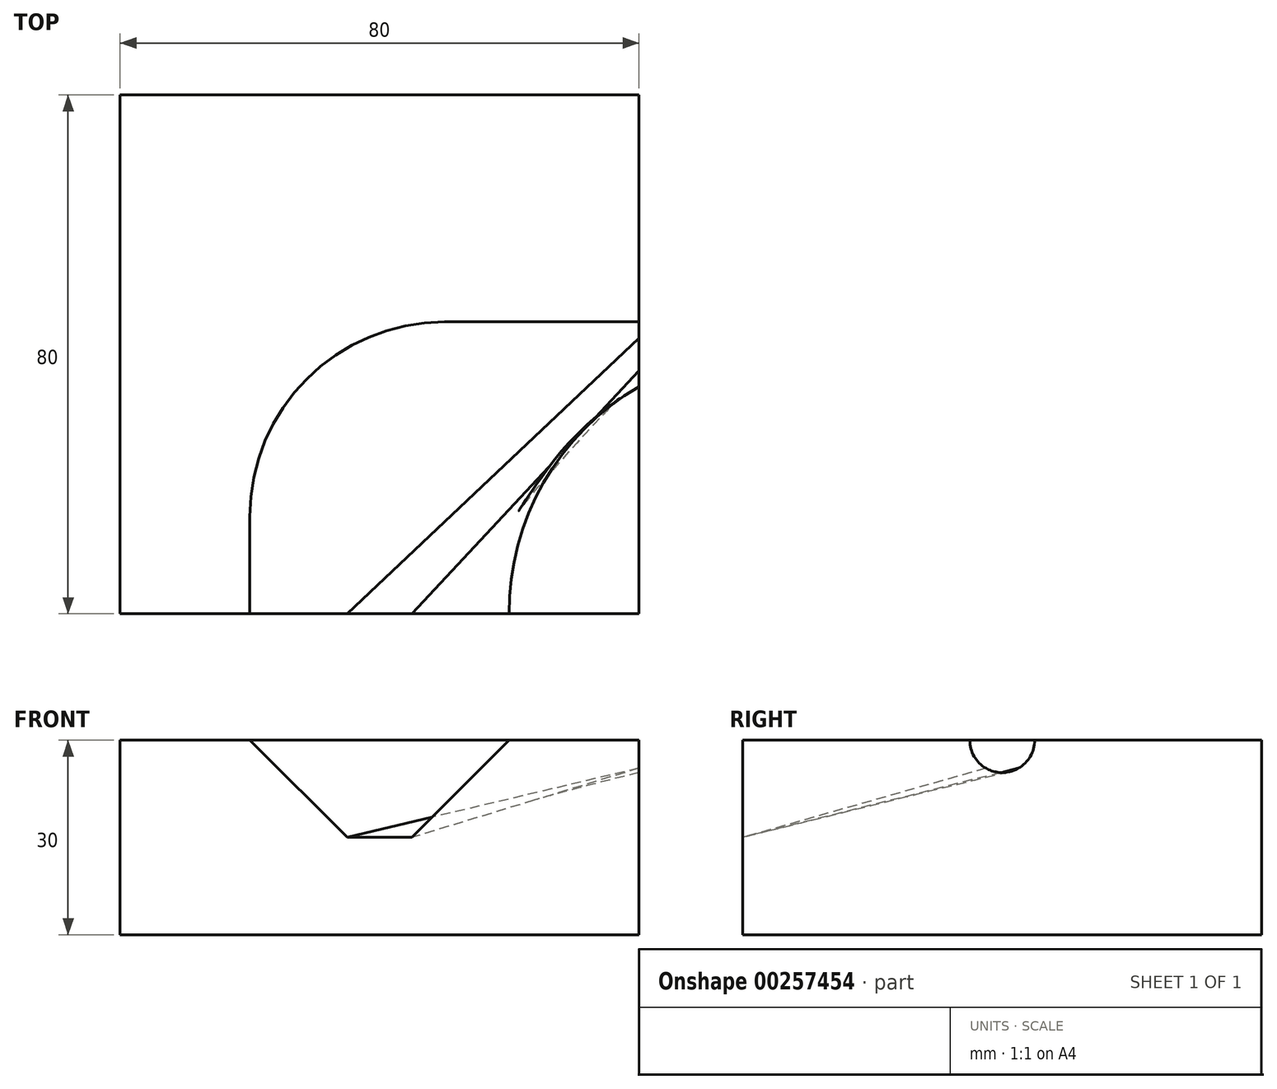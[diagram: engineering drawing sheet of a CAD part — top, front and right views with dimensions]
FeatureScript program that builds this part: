
annotation { "Feature Type Name" : "Feature", "Feature Type Description" : "" }
export const myFeature = defineFeature(function(context is Context, id is Id, definition is map)
    precondition{}
    {
        {
            var Q0;
            Q0=qCreatedBy(makeId("Top.planeOp"),FACE);
            var sketch = newSketch(context, id + "F0", { "sketchPlane" : qUnion([Q0])});
            skLineSegment(sketch, "E0.bottom", {"start": v(40, 40) * mm, "end": v(-40, 40) * mm});
            skLineSegment(sketch, "E0.top", {"start": v(40, -40) * mm, "end": v(-40, -40) * mm});
            skLineSegment(sketch, "E0.left", {"start": v(40, 40) * mm, "end": v(40, -40) * mm});
            skLineSegment(sketch, "E0.right", {"start": v(-40, 40) * mm, "end": v(-40, -40) * mm});
            skPoint(sketch, "E0.middle", {"position": v(0, 0) * mm});
            skArc(sketch, "E1", {"start": v(40, -5) * mm, "mid": v(25.27, -19.8) * mm, "end": v(20, -40) * mm});
            skLineSegment(sketch, "E2", {"start": v(-20, -40) * mm, "end": v(-20, -25) * mm});
            skLineSegment(sketch, "E3", {"start": v(40, 5) * mm, "end": v(10, 5) * mm});
            skArc(sketch, "E4", {"start": v(10, 5) * mm, "mid": v(-11.21, -3.79) * mm, "end": v(-20, -25) * mm});
            skSolve(sketch);
        }
        {
            var Q0;
            {var subQ2=sQuery(id+"F0.wireOp",EDGE,"E0.bottom");Q0=makeQuery(id+"F0.imprint","IMPRINT",FACE,{"disambiguationData":[TD([[makeQuery(id+"F0.imprint","IMPRINT",EDGE,{"derivedFrom":subQ2}),1.0]])]});}
            var Q1;
            {var subQ1=sQuery(id+"F0.wireOp",EDGE,"E1");Q1=makeQuery(id+"F0.imprint","IMPRINT",FACE,{"disambiguationData":[TD([[makeQuery(id+"F0.imprint","IMPRINT",EDGE,{"derivedFrom":subQ1}),-1.0]])]});}
            var Q2;
            {var subQ3=sQuery(id+"F0.wireOp",EDGE,"E1");Q2=makeQuery(id+"F0.imprint","IMPRINT",FACE,{"disambiguationData":[TD([[makeQuery(id+"F0.imprint","IMPRINT",EDGE,{"derivedFrom":subQ3}),1.0]])]});}
            extrude(context, id + "F1", {"entities" : qUnion([Q0, Q1, Q2]), "oppositeDirection" : true, "depth" : 30 * mm});
        }
        {
            var Q0;
            Q0=makeQuery(id+"F1.opExtrude","SWEPT_FACE",FACE,{"disambiguationData":[OSD([sQuery(id+"F0.wireOp",EDGE,"E0.left")])]});
            var sketch = newSketch(context, id + "F2", { "sketchPlane" : qUnion([Q0])});
            skLineSegment(sketch, "E5.0", {"start": v(-5, 0) * mm, "end": v(-40, 0) * mm});
            skPoint(sketch, "E6.0", {"position": v(5, 0) * mm});
            skLineSegment(sketch, "E7.0", {"start": v(5, 0) * mm, "end": v(-25, 0) * mm});
            skLineSegment(sketch, "E8.0", {"start": v(40, 0) * mm, "end": v(-40, 0) * mm});
            skArc(sketch, "E9", {"start": v(-5, 0) * mm, "mid": v(0, -5) * mm, "end": v(5, 0) * mm});
            skSolve(sketch);
        }
        {
            var Q0;
            Q0=makeQuery(id+"F1.opExtrude","SWEPT_FACE",FACE,{"disambiguationData":[OSD([sQuery(id+"F0.wireOp",EDGE,"E0.top")])]});
            var sketch = newSketch(context, id + "F3", { "sketchPlane" : qUnion([Q0])});
            skPoint(sketch, "E10.0", {"position": v(-20, 0) * mm});
            skPoint(sketch, "E11.0", {"position": v(20, 0) * mm});
            skLineSegment(sketch, "E12", {"start": v(-20, 0) * mm, "end": v(-5, -15) * mm});
            skLineSegment(sketch, "E13", {"start": v(-5, -15) * mm, "end": v(5, -15) * mm});
            skLineSegment(sketch, "E14", {"start": v(5, -15) * mm, "end": v(20, 0) * mm});
            skSolve(sketch);
        }
        {
            var Q0;
            {var subQ2=sQuery(id+"F0.wireOp",EDGE,"E0.bottom");Q0=makeQuery(id+"F0.imprint","IMPRINT",FACE,{"disambiguationData":[TD([[makeQuery(id+"F0.imprint","IMPRINT",EDGE,{"derivedFrom":subQ2}),1.0]])]});}
            var sketch = newSketch(context, id + "F4", { "sketchPlane" : qUnion([Q0])});
            skLineSegment(sketch, "E15.0", {"start": v(40, 5) * mm, "end": v(10, 5) * mm});
            skArc(sketch, "E16.0", {"start": v(10, 5) * mm, "mid": v(-11.21, -3.79) * mm, "end": v(-20, -25) * mm});
            skLineSegment(sketch, "E17.0", {"start": v(-20, -40) * mm, "end": v(-20, -25) * mm});
            skSolve(sketch);
        }
        {
            var Q1;
            {var subQ0=sQuery(id+"F2.wireOp",EDGE,"E9");Q1=makeQuery(id+"F2.imprint","IMPRINT",FACE,{"disambiguationData":[TD([[makeQuery(id+"F2.imprint","IMPRINT",EDGE,{"derivedFrom":subQ0}),1.0]])]});}
            var Q2;
            {var subQ0=sQuery(id+"F3.wireOp",EDGE,"E12");Q2=makeQuery(id+"F3.imprint","IMPRINT",FACE,{"disambiguationData":[TD([[makeQuery(id+"F3.imprint","IMPRINT",EDGE,{"derivedFrom":subQ0}),1.0]])]});}
            var Q3;
            Q3 = qConstructionFilter(qBodyType(qCreatedBy(id + "F4" ,EDGE), BodyType.WIRE), ConstructionObject.NO);
            var Q4;
            Q4=sQuery(id+"F0.wireOp",EDGE,"E1");
            loft(context, id + "F5", {"operationType" : NewBodyOperationType.REMOVE, "addGuides" : true, "sheetProfilesArray" : [{ "sheetProfileEntities" : qUnion([Q1]) }, { "sheetProfileEntities" : qUnion([Q2]) }], "guidesArray" : [{ "guideEntities" : qUnion([Q3]), "guideDerivativeType" : LoftGuideDerivativeType.DEFAULT, "guideDerivativeMagnitude" : 1 }, { "guideEntities" : qUnion([Q4]), "guideDerivativeType" : LoftGuideDerivativeType.DEFAULT, "guideDerivativeMagnitude" : 1 }]});
        }
    });
